# Revit family: Bomsystem1 sammansatt
name_source: partatom
category: Generic Models
revit_build: Autodesk Revit 2017 (Build: 20160225_1515(x64)
units: mm (PartAtom-declared; Revit-internal decimal feet)

## family parameters
Always vertical = Yes
Can host rebar = No
Cut with Voids When Loaded = No
Part Type = Normal
Room Calculation Point = No
Round Connector Dimension = Use Diameter
Shared = No
Work Plane-Based = No

## types (4) — shared parameters
Manufacturer = Saxi Vägg AB
Model = Saxi Bomsystem 1
URL = www.saxi.se

## per-type parameters (varying)
| type | 2 | H | Height | Height_stolpe | Height_stolpe2 | V | to_middle_support |
| Saxi Bomsystem 1 V | No | No | 9000 mm | 8940 mm  [stored 29.3307 ft] | 7800 mm  [stored 25.5906 ft] | Yes | 4500 mm |
| Saxi Bomsystem 1 H | No | Yes | 9000 mm | 8940 mm  [stored 29.3307 ft] | 7800 mm  [stored 25.5906 ft] | No | 4500 mm |
| Saxi Bomsystem 2 V | Yes | No | 9000 mm | 8940 mm  [stored 29.3307 ft] | 7800 mm  [stored 25.5906 ft] | Yes | 4500 mm |
| Saxi Bomsystem 2 H | Yes | Yes | 8000 mm  [stored 26.2467 ft] | 7940 mm  [stored 26.0499 ft] | 6800 mm  [stored 22.3097 ft] | No | 4000 mm  [stored 13.1234 ft] |

note: [stored X ft] marks values corroborated as IEEE doubles in the binary element streams (Revit-internal decimal feet)

## geometry (parser evidence)
native form markers: Sweep x37
no freeform markers — native parametric forms only
